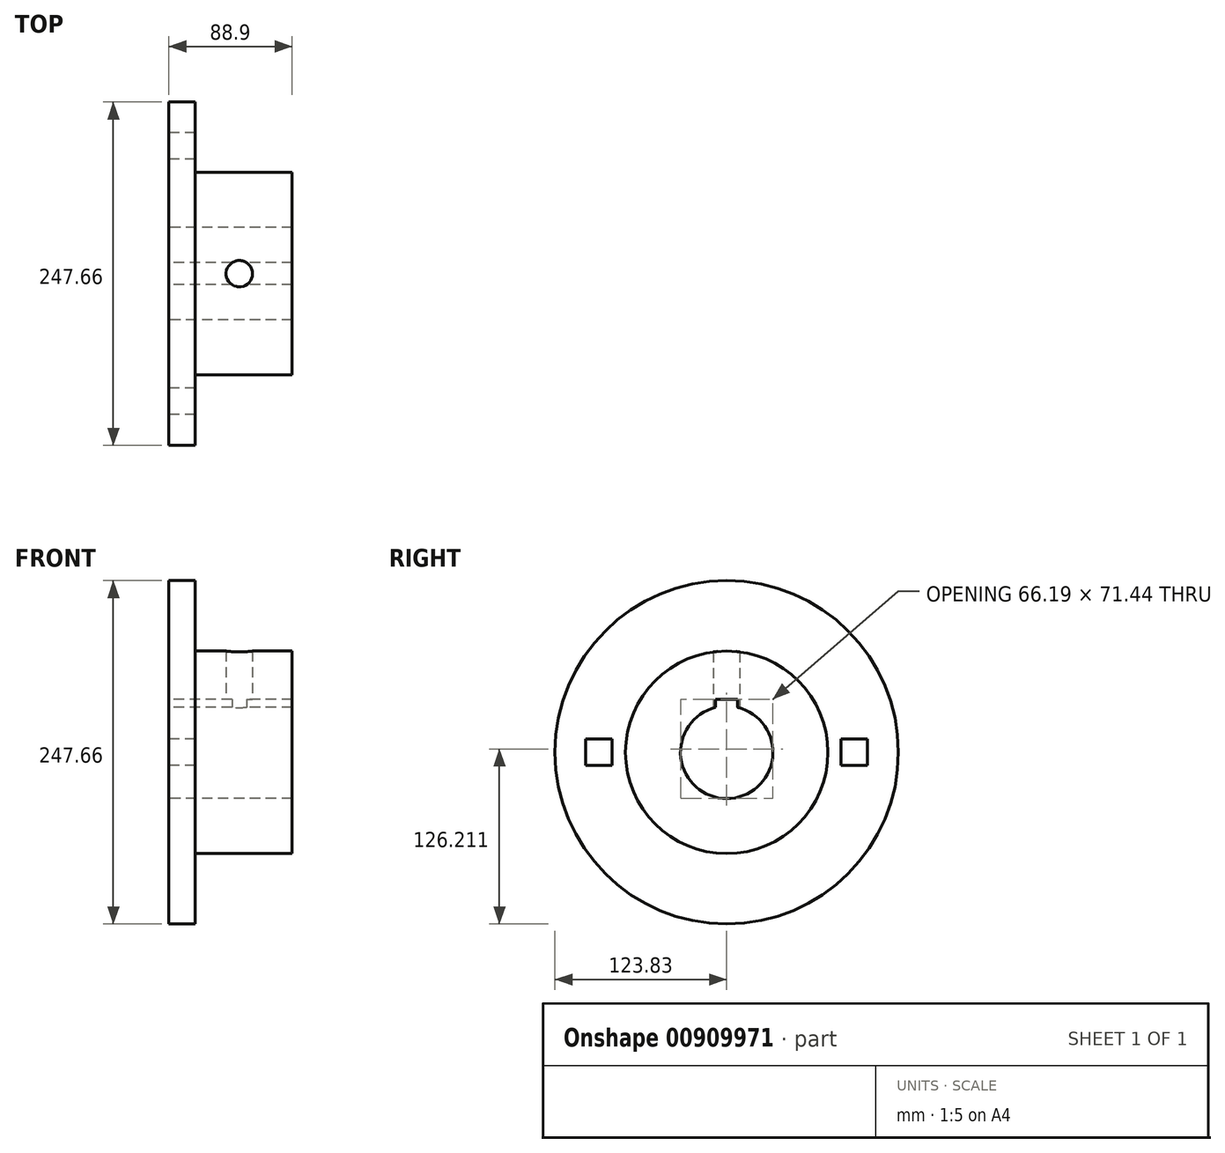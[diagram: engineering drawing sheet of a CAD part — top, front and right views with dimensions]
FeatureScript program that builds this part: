
annotation { "Feature Type Name" : "Feature", "Feature Type Description" : "" }
export const myFeature = defineFeature(function(context is Context, id is Id, definition is map)
    precondition{}
    {
        {
            var Q0;
            Q0=qCreatedBy(makeId("Right.planeOp"),FACE);
            var sketch = newSketch(context, id + "F0", { "sketchPlane" : qUnion([Q0])});
            skCircle(sketch, "E0", {"center": v(0, 0) * mm, "radius": 73.03 * mm});
            skCircle(sketch, "E1", {"center": v(0, 0) * mm, "radius": 33.34 * mm});
            skLineSegment(sketch, "E2.bottom", {"start": v(-7.94, 38.1) * mm, "end": v(7.94, 38.1) * mm});
            skLineSegment(sketch, "E2.top", {"start": v(-7.94, 25.4) * mm, "end": v(7.94, 25.4) * mm});
            skLineSegment(sketch, "E2.left", {"start": v(-7.94, 38.1) * mm, "end": v(-7.94, 25.4) * mm});
            skLineSegment(sketch, "E2.right", {"start": v(7.94, 38.1) * mm, "end": v(7.94, 25.4) * mm});
            skLineSegment(sketch, "E3", {"start": v(0, 38.1) * mm, "end": v(0, 0) * mm, "construction": true});
            skLineSegment(sketch, "E4.bottom", {"start": v(-101.6, 9.52) * mm, "end": v(-82.55, 9.52) * mm});
            skLineSegment(sketch, "E4.top", {"start": v(-101.6, -9.52) * mm, "end": v(-82.55, -9.52) * mm});
            skLineSegment(sketch, "E4.left", {"start": v(-101.6, 9.52) * mm, "end": v(-101.6, -9.52) * mm});
            skLineSegment(sketch, "E4.right", {"start": v(-82.55, 9.52) * mm, "end": v(-82.55, 0) * mm});
            skLineSegment(sketch, "E5.bottom", {"start": v(82.55, 9.52) * mm, "end": v(101.6, 9.52) * mm});
            skLineSegment(sketch, "E5.top", {"start": v(82.55, -9.52) * mm, "end": v(101.6, -9.52) * mm});
            skLineSegment(sketch, "E5.left", {"start": v(82.55, 9.52) * mm, "end": v(82.55, 0) * mm});
            skLineSegment(sketch, "E5.right", {"start": v(101.6, 9.52) * mm, "end": v(101.6, -9.53) * mm});
            skPoint(sketch, "E6", {"position": v(-82.55, 0) * mm});
            skLineSegment(sketch, "E7", {"start": v(0, 0) * mm, "end": v(82.55, 0) * mm, "construction": true});
            skLineSegment(sketch, "E8", {"start": v(-82.55, 0) * mm, "end": v(-82.55, -9.52) * mm});
            skLineSegment(sketch, "E9", {"start": v(-82.55, 0) * mm, "end": v(0, 0) * mm, "construction": true});
            skLineSegment(sketch, "E10", {"start": v(82.55, 0) * mm, "end": v(82.55, -9.52) * mm});
            skCircle(sketch, "E11.converted", {"center": v(0, 0) * mm, "radius": 123.83 * mm});
            skSolve(sketch);
        }
        {
            var Q0;
            Q0=makeQuery(id+"F0.imprint","IMPRINT",FACE,{"disambiguationData":[TD([[makeQuery(id+"F0.imprint","IMPRINT",EDGE,{"derivedFrom":sQuery(id+"F0.wireOp",EDGE,"E0")}),1.0]])]});
            extrude(context, id + "F1", {"entities" : qUnion([Q0]), "depth" : 88.9 * mm, "offsetDistance" : 25 * mm});
        }
        {
            var Q0;
            Q0=makeQuery(id+"F0.imprint","IMPRINT",FACE,{"disambiguationData":[TD([[makeQuery(id+"F0.imprint","IMPRINT",EDGE,{"derivedFrom":sQuery(id+"F0.wireOp",EDGE,"E0")}),-1.0]])]});
            extrude(context, id + "F2", {"entities" : qUnion([Q0]), "operationType" : NewBodyOperationType.ADD, "depth" : 19.05 * mm, "offsetDistance" : 25 * mm});
        }
        {
            var Q0;
            Q0=qCreatedBy(makeId("Top.planeOp"),FACE);
            var sketch = newSketch(context, id + "F3", { "sketchPlane" : qUnion([Q0])});
            skCircle(sketch, "E12", {"center": v(50.8, 0) * mm, "radius": 9.53 * mm});
            skSolve(sketch);
        }
        {
            var Q0;
            Q0=makeQuery(id+"F3.imprint","IMPRINT",FACE,{"disambiguationData":[TD([[makeQuery(id+"F3.imprint","IMPRINT",EDGE,{"derivedFrom":sQuery(id+"F3.wireOp",EDGE,"E12")}),1.0]])]});
            extrude(context, id + "F4", {"entities" : qUnion([Q0]), "operationType" : NewBodyOperationType.REMOVE, "endBound" : BoundingType.THROUGH_ALL, "depth" : 25 * mm, "offsetDistance" : 25 * mm});
        }
    });
